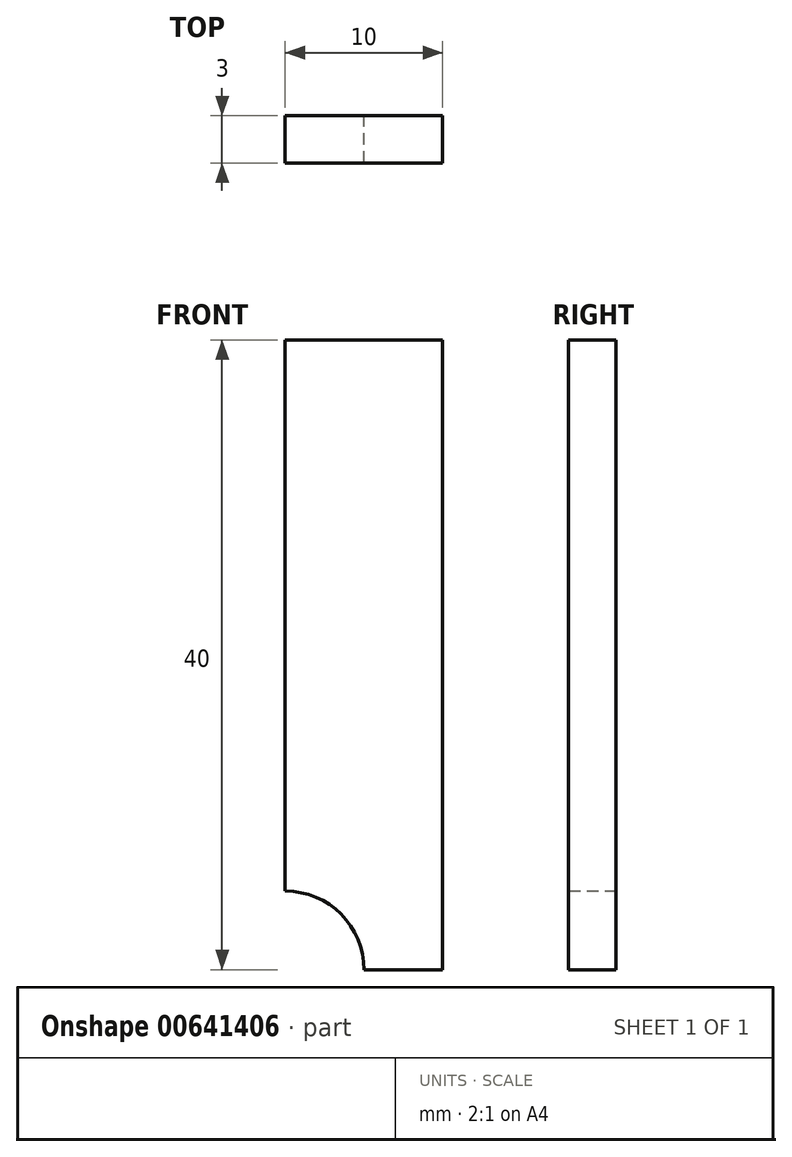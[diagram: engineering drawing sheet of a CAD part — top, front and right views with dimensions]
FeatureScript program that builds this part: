
annotation { "Feature Type Name" : "Feature", "Feature Type Description" : "" }
export const myFeature = defineFeature(function(context is Context, id is Id, definition is map)
    precondition{}
    {
        {
            var Q0;
            Q0=qCreatedBy(makeId("Front.planeOp"),FACE);
            var sketch = newSketch(context, id + "F0", { "sketchPlane" : qUnion([Q0])});
            skLineSegment(sketch, "E0.bottom", {"start": v(0, 0) * mm, "end": v(10, 0) * mm});
            skLineSegment(sketch, "E0.top", {"start": v(0, 40) * mm, "end": v(10, 40) * mm});
            skLineSegment(sketch, "E0.left", {"start": v(0, 0) * mm, "end": v(0, 40) * mm});
            skLineSegment(sketch, "E0.right", {"start": v(10, 0) * mm, "end": v(10, 40) * mm});
            skArc(sketch, "E1", {"start": v(0, 5) * mm, "mid": v(3.54, 3.54) * mm, "end": v(5, 0) * mm});
            skSolve(sketch);
        }
        {
            var Q0;
            {var subQ2=sQuery(id+"F0.wireOp",EDGE,"E0.top");Q0=makeQuery(id+"F0.imprint","IMPRINT",FACE,{"disambiguationData":[TD([[makeQuery(id+"F0.imprint","IMPRINT",EDGE,{"derivedFrom":subQ2}),-1.0]])]});}
            extrude(context, id + "F1", {"entities" : qUnion([Q0]), "depth" : 3 * mm, "offsetDistance" : 25 * mm});
        }
    });
